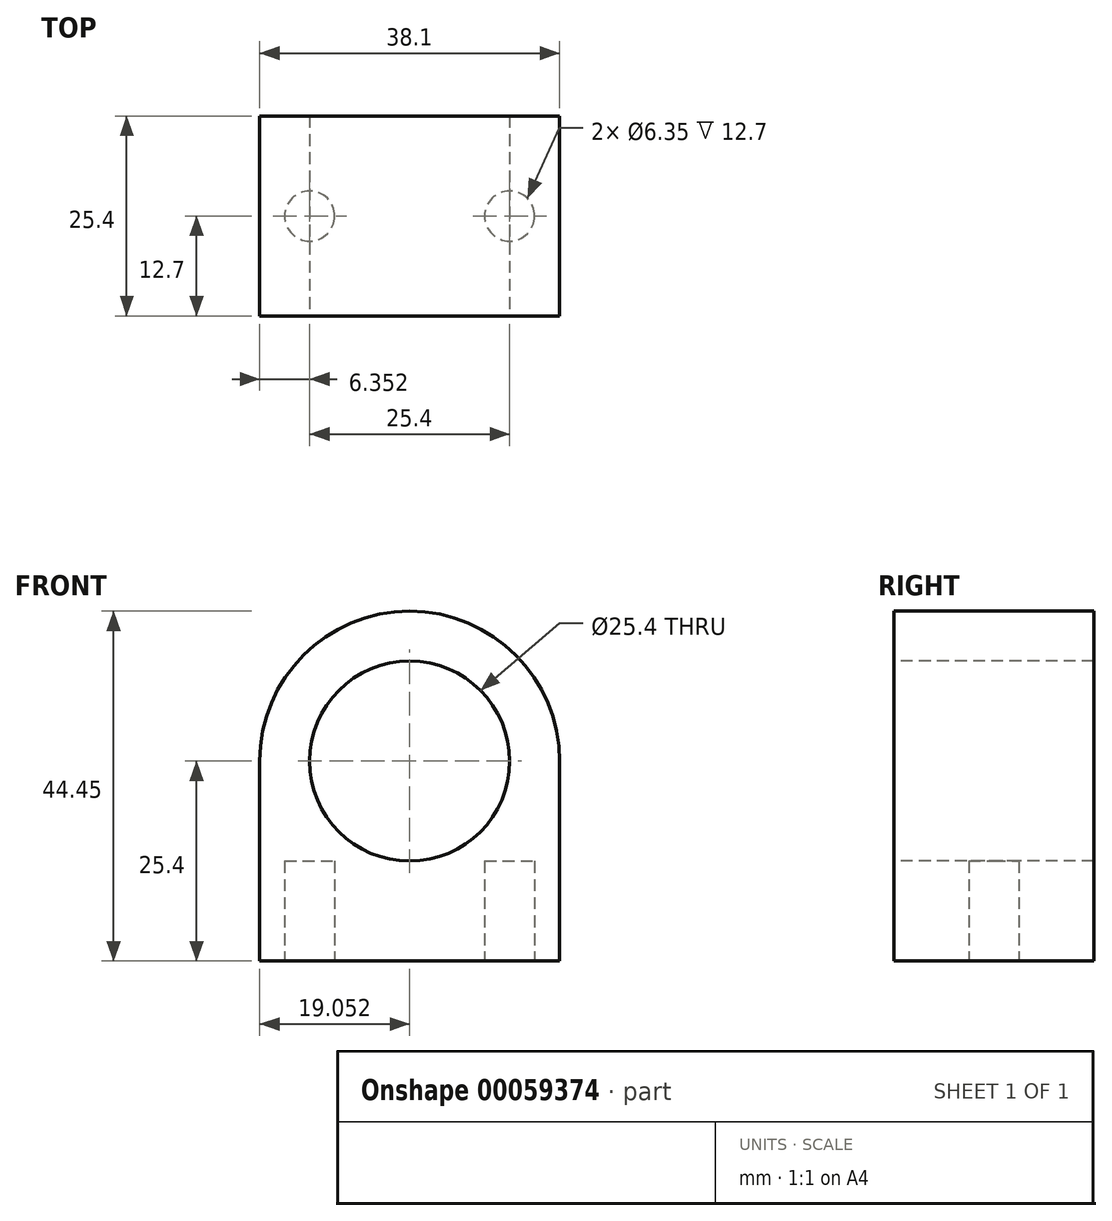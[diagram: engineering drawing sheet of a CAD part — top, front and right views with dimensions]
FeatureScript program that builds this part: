
annotation { "Feature Type Name" : "Feature", "Feature Type Description" : "" }
export const myFeature = defineFeature(function(context is Context, id is Id, definition is map)
    precondition{}
    {
        {
            var Q0;
            Q0=qCreatedBy(makeId("Front.planeOp"),FACE);
            var sketch = newSketch(context, id + "F0", { "sketchPlane" : qUnion([Q0])});
            skLineSegment(sketch, "E0.bottom", {"start": v(-7.07, 0) * mm, "end": v(31.03, 0) * mm});
            skLineSegment(sketch, "E0.top", {"start": v(11.98, 44.45) * mm, "end": v(11.98, 44.45) * mm});
            skLineSegment(sketch, "E0.left", {"start": v(-7.07, 0) * mm, "end": v(-7.07, 25.4) * mm});
            skLineSegment(sketch, "E0.right", {"start": v(31.03, 0) * mm, "end": v(31.03, 25.4) * mm});
            skPoint(sketch, "E1.visualSharp", {"position": v(-7.07, 44.45) * mm});
            skArc(sketch, "E1.filletArc", {"start": v(11.98, 44.45) * mm, "mid": v(-1.49, 38.87) * mm, "end": v(-7.07, 25.4) * mm});
            skPoint(sketch, "E2.visualSharp", {"position": v(31.03, 44.45) * mm});
            skArc(sketch, "E2.filletArc", {"start": v(31.03, 25.4) * mm, "mid": v(25.45, 38.87) * mm, "end": v(11.98, 44.45) * mm});
            skSolve(sketch);
        }
        {
            var Q0;
            Q0 = qSketchRegion(id + "F0", true);
            extrude(context, id + "F1", {"entities" : qUnion([Q0]), "depth" : 25.4 * mm});
        }
        {
            var Q0;
            Q0=makeQuery(id+"F1.opExtrude","CAP_FACE",FACE,{"disambiguationData":[OSD([sQuery(id+"F0.wireOp",EDGE,"E0.bottom"),sQuery(id+"F0.wireOp",EDGE,"E0.left"),sQuery(id+"F0.wireOp",EDGE,"E0.right"),sQuery(id+"F0.wireOp",EDGE,"E1.filletArc"),sQuery(id+"F0.wireOp",EDGE,"E2.filletArc")])],"isStart":false});
            var sketch = newSketch(context, id + "F2", { "sketchPlane" : qUnion([Q0])});
            skCircle(sketch, "E3", {"center": v(11.98, 25.4) * mm, "radius": 12.7 * mm});
            skSolve(sketch);
        }
        {
            var Q0;
            Q0=makeQuery(id+"F2.imprint","IMPRINT",FACE,{"disambiguationData":[TD([[makeQuery(id+"F2.imprint","IMPRINT",EDGE,{"derivedFrom":sQuery(id+"F2.wireOp",EDGE,"E3")}),1.0]])]});
            extrude(context, id + "F3", {"entities" : qUnion([Q0]), "operationType" : NewBodyOperationType.REMOVE, "oppositeDirection" : true, "depth" : 61.58 * mm});
        }
        {
            var Q0;
            Q0=makeQuery(id+"F1.opExtrude","SWEPT_FACE",FACE,{"disambiguationData":[OSD([sQuery(id+"F0.wireOp",EDGE,"E0.bottom")])]});
            var sketch = newSketch(context, id + "F4", { "sketchPlane" : qUnion([Q0])});
            skCircle(sketch, "E4", {"center": v(-0.72, 12.7) * mm, "radius": 3.18 * mm});
            skCircle(sketch, "E5", {"center": v(24.68, 12.7) * mm, "radius": 3.18 * mm});
            skSolve(sketch);
        }
        {
            var Q0;
            Q0 = qSketchRegion(id + "F4", true);
            extrude(context, id + "F5", {"entities" : qUnion([Q0]), "operationType" : NewBodyOperationType.REMOVE, "oppositeDirection" : true, "depth" : 12.7 * mm});
        }
    });
